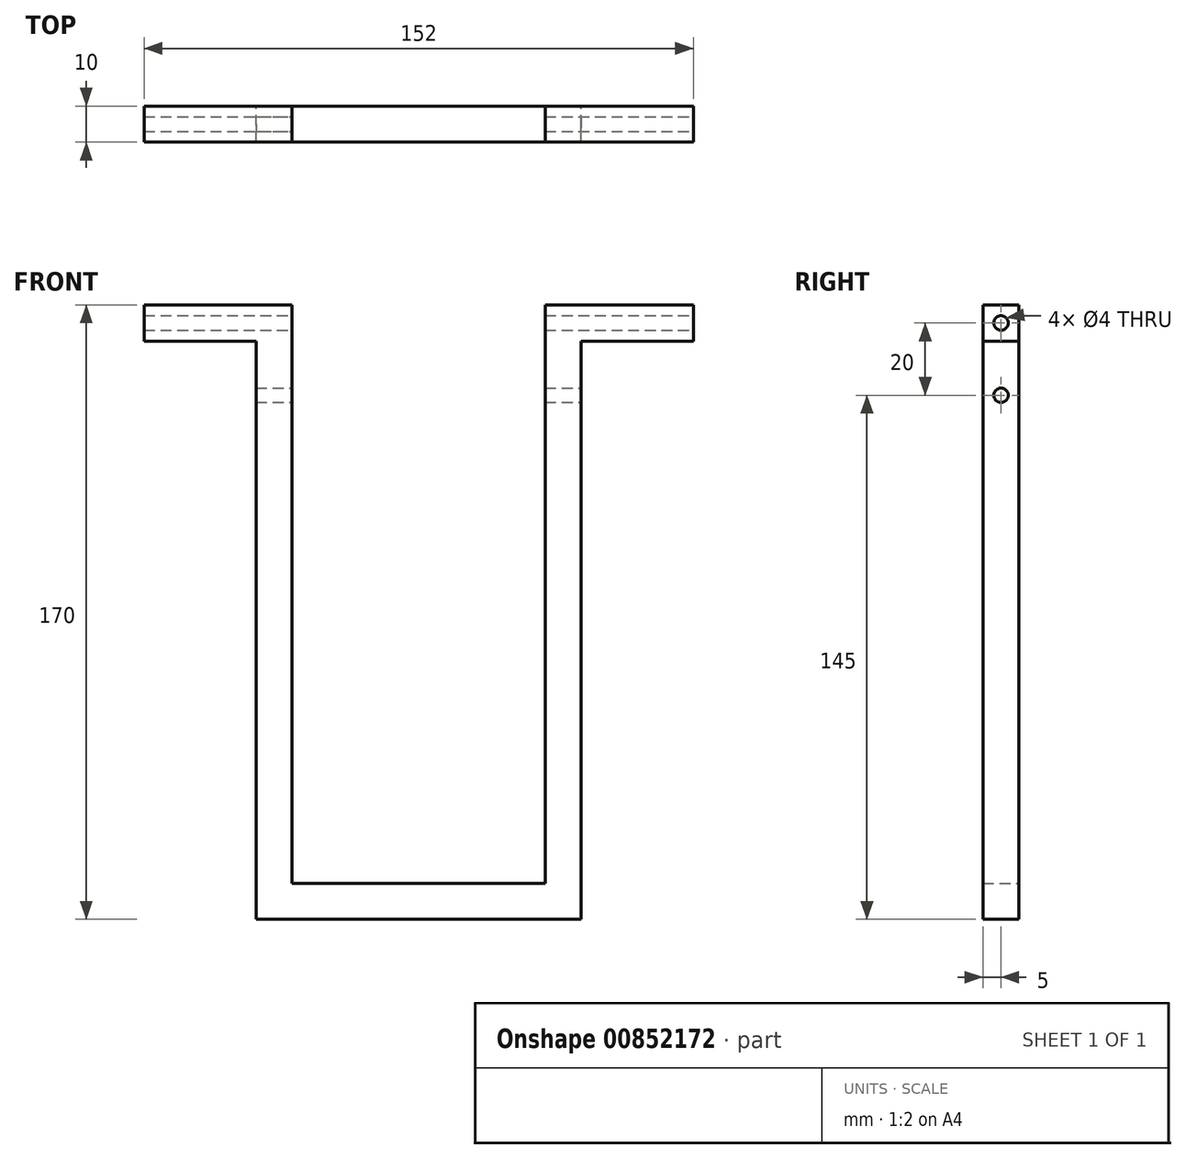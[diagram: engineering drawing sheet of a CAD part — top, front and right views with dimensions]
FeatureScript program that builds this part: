
annotation { "Feature Type Name" : "Feature", "Feature Type Description" : "" }
export const myFeature = defineFeature(function(context is Context, id is Id, definition is map)
    precondition{}
    {
        {
            var Q0;
            Q0=qCreatedBy(makeId("Front.planeOp"),FACE);
            var sketch = newSketch(context, id + "F0", { "sketchPlane" : qUnion([Q0])});
            skLineSegment(sketch, "E0", {"start": v(-45, -15) * mm, "end": v(-45, 145) * mm});
            skLineSegment(sketch, "E1", {"start": v(-35, 155) * mm, "end": v(-35, -5) * mm});
            skLineSegment(sketch, "E2", {"start": v(-35, -5) * mm, "end": v(0, -5) * mm});
            skLineSegment(sketch, "E3.MirrorCS", {"start": v(35, 155) * mm, "end": v(35, -5) * mm});
            skLineSegment(sketch, "E4.MirrorCS", {"start": v(35, -5) * mm, "end": v(0, -5) * mm});
            skLineSegment(sketch, "E5", {"start": v(-45, -15) * mm, "end": v(45, -15) * mm});
            skLineSegment(sketch, "E6", {"start": v(-76, 155) * mm, "end": v(-76, 145) * mm});
            skLineSegment(sketch, "E7", {"start": v(-76, 145) * mm, "end": v(-45, 145) * mm});
            skLineSegment(sketch, "E8", {"start": v(-76, 155) * mm, "end": v(-35, 155) * mm});
            skLineSegment(sketch, "E9", {"start": v(-45, 145) * mm, "end": v(-35, 145) * mm, "construction": true});
            skLineSegment(sketch, "E10.MirrorCS", {"start": v(76, 155) * mm, "end": v(35, 155) * mm});
            skLineSegment(sketch, "E11.MirrorCS", {"start": v(76, 155) * mm, "end": v(76, 145) * mm});
            skLineSegment(sketch, "E12.MirrorCS", {"start": v(45, -15) * mm, "end": v(45, 145) * mm});
            skLineSegment(sketch, "E13.MirrorCS", {"start": v(76, 145) * mm, "end": v(45, 145) * mm});
            skLineSegment(sketch, "E14", {"start": v(0, -5) * mm, "end": v(0, -15) * mm, "construction": true});
            skSolve(sketch);
        }
        {
            var Q0;
            Q0 = qSketchRegion(id + "F0", true);
            extrude(context, id + "F1", {"entities" : qUnion([Q0]), "depth" : 10 * mm, "offsetDistance" : 25 * mm});
        }
        {
            var Q0;
            Q0=makeQuery(id+"F1.opExtrude","SWEPT_FACE",FACE,{"disambiguationData":[OSD([sQuery(id+"F0.wireOp",EDGE,"E11.MirrorCS")])]});
            var sketch = newSketch(context, id + "F2", { "sketchPlane" : qUnion([Q0])});
            skLineSegment(sketch, "E15", {"start": v(-10, 155) * mm, "end": v(0, 145) * mm, "construction": true});
            skCircle(sketch, "E16", {"center": v(-5, 150) * mm, "radius": 2 * mm});
            skSolve(sketch);
        }
        {
            var Q0;
            Q0 = qSketchRegion(id + "F2", true);
            extrude(context, id + "F3", {"entities" : qUnion([Q0]), "operationType" : NewBodyOperationType.REMOVE, "endBound" : BoundingType.THROUGH_ALL, "oppositeDirection" : true, "depth" : 25 * mm, "offsetDistance" : 25 * mm});
        }
        {
            var Q0;
            Q0=makeQuery(id+"F1.opExtrude","SWEPT_FACE",FACE,{"disambiguationData":[OSD([sQuery(id+"F0.wireOp",EDGE,"E12.MirrorCS")])]});
            var sketch = newSketch(context, id + "F4", { "sketchPlane" : qUnion([Q0])});
            skLineSegment(sketch, "E17", {"start": v(-10, 130) * mm, "end": v(0, 130) * mm, "construction": true});
            skCircle(sketch, "E18", {"center": v(-5, 130) * mm, "radius": 2 * mm});
            skSolve(sketch);
        }
        {
            var Q0;
            Q0 = qSketchRegion(id + "F4", true);
            extrude(context, id + "F5", {"entities" : qUnion([Q0]), "operationType" : NewBodyOperationType.REMOVE, "endBound" : BoundingType.THROUGH_ALL, "oppositeDirection" : true, "depth" : 25 * mm, "offsetDistance" : 25 * mm});
        }
    });
